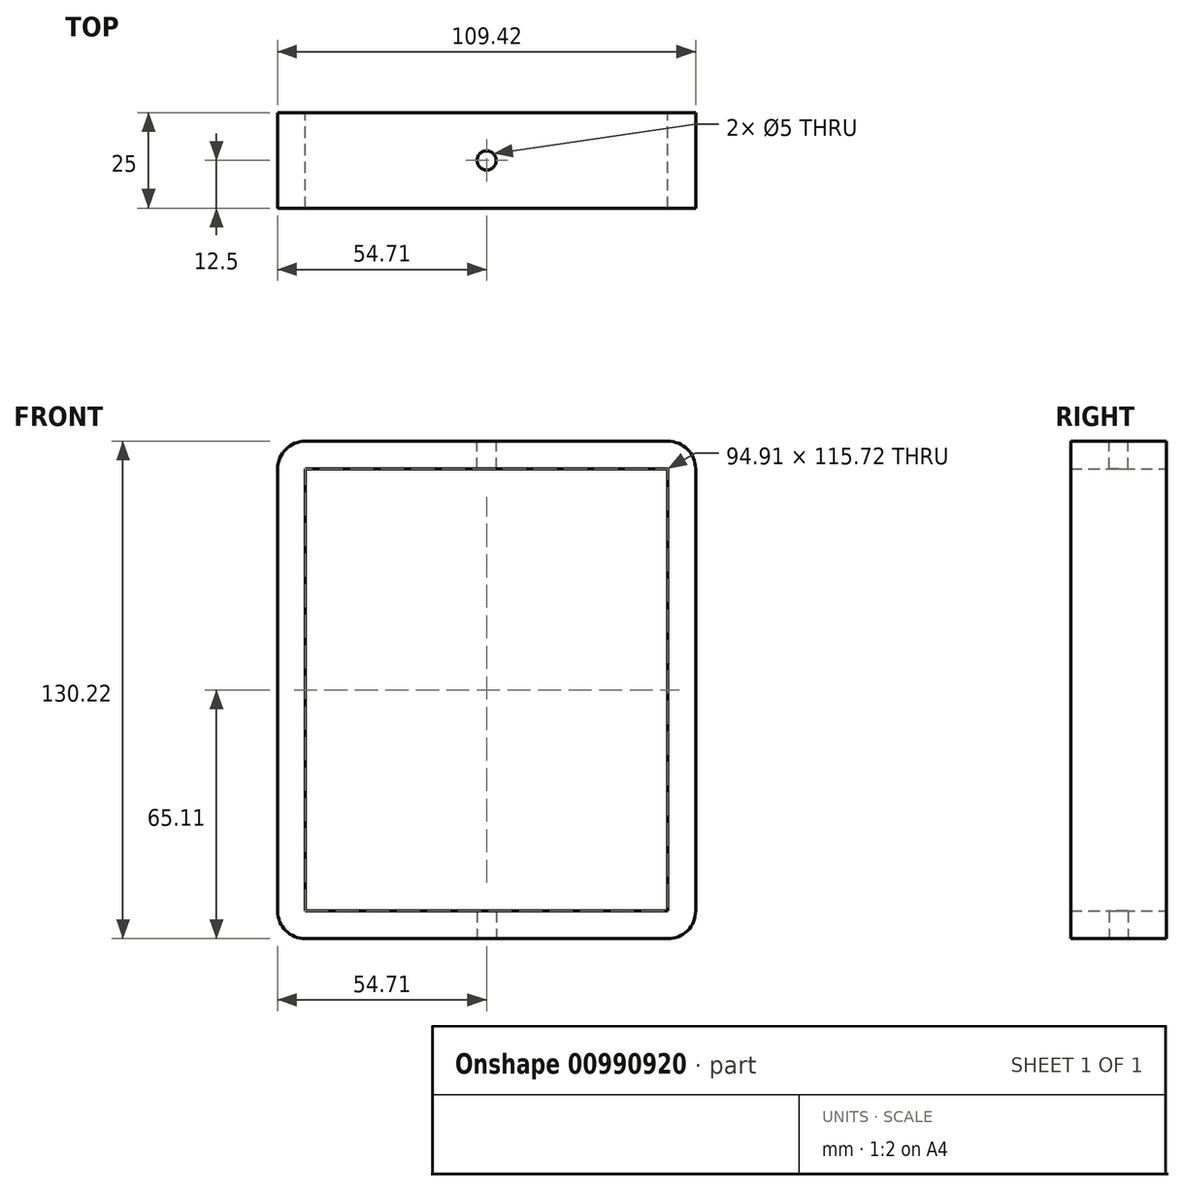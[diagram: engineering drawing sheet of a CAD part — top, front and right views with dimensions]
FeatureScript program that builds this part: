
annotation { "Feature Type Name" : "Feature", "Feature Type Description" : "" }
export const myFeature = defineFeature(function(context is Context, id is Id, definition is map)
    precondition{}
    {
        {
            var Q0;
            Q0=qCreatedBy(makeId("Front.planeOp"),FACE);
            var sketch = newSketch(context, id + "F0", { "sketchPlane" : qUnion([Q0])});
            skLineSegment(sketch, "E0.bottom", {"start": v(47.45, 57.86) * mm, "end": v(-47.45, 57.86) * mm});
            skLineSegment(sketch, "E0.top", {"start": v(47.45, 65.11) * mm, "end": v(-47.45, 65.11) * mm});
            skLineSegment(sketch, "E0.left", {"start": v(47.45, 57.86) * mm, "end": v(47.45, 65.11) * mm});
            skLineSegment(sketch, "E0.right", {"start": v(-47.45, 57.86) * mm, "end": v(-47.45, 65.11) * mm, "construction": true});
            skPoint(sketch, "E0.middle", {"position": v(0, 61.49) * mm});
            skLineSegment(sketch, "E1.MirrorCS", {"start": v(-47.45, -57.86) * mm, "end": v(-47.45, -65.11) * mm});
            skLineSegment(sketch, "E2.MirrorCS", {"start": v(47.45, -65.11) * mm, "end": v(-47.45, -65.11) * mm});
            skLineSegment(sketch, "E3.MirrorCS", {"start": v(47.45, -57.86) * mm, "end": v(47.45, -65.11) * mm, "construction": true});
            skLineSegment(sketch, "E4.MirrorCS", {"start": v(47.45, -57.86) * mm, "end": v(-47.45, -57.86) * mm});
            skArc(sketch, "E5", {"start": v(54.7, -57.86) * mm, "mid": v(52.58, -62.99) * mm, "end": v(47.45, -65.11) * mm});
            skArc(sketch, "E6", {"start": v(-54.7, 57.86) * mm, "mid": v(-52.58, 62.99) * mm, "end": v(-47.45, 65.11) * mm});
            skArc(sketch, "E7", {"start": v(47.45, 65.11) * mm, "mid": v(52.58, 62.99) * mm, "end": v(54.7, 57.86) * mm});
            skArc(sketch, "E8", {"start": v(-47.45, -65.11) * mm, "mid": v(-52.58, -62.99) * mm, "end": v(-54.7, -57.86) * mm});
            skLineSegment(sketch, "E9", {"start": v(-47.45, 57.86) * mm, "end": v(-47.45, -57.86) * mm});
            skLineSegment(sketch, "E10", {"start": v(-54.7, 57.86) * mm, "end": v(-54.7, -57.86) * mm});
            skLineSegment(sketch, "E11", {"start": v(47.45, 57.86) * mm, "end": v(47.45, -57.86) * mm});
            skLineSegment(sketch, "E12", {"start": v(54.7, 57.86) * mm, "end": v(54.7, -57.86) * mm});
            skSolve(sketch);
        }
        {
            var Q0;
            Q0 = qSketchRegion(id + "F0", true);
            extrude(context, id + "F1", {"entities" : qUnion([Q0]), "depth" : 25 * mm, "offsetDistance" : 25 * mm});
        }
        {
            var Q0;
            Q0=makeQuery(id+"F1.opExtrude","SWEPT_FACE",FACE,{"disambiguationData":[OSD([sQuery(id+"F0.wireOp",EDGE,"E0.top")])]});
            var sketch = newSketch(context, id + "F2", { "sketchPlane" : qUnion([Q0])});
            skPoint(sketch, "E13", {"position": v(-47.45, -12.5) * mm});
            skLineSegment(sketch, "E14", {"start": v(-47.45, -12.5) * mm, "end": v(47.45, -12.5) * mm, "construction": true});
            skCircle(sketch, "E15", {"center": v(0, -12.5) * mm, "radius": 2.5 * mm});
            skSolve(sketch);
        }
        {
            var Q0;
            Q0=makeQuery(id+"F1.opExtrude","SWEPT_FACE",FACE,{"disambiguationData":[OSD([sQuery(id+"F0.wireOp",EDGE,"E2.MirrorCS")])]});
            var sketch = newSketch(context, id + "F3", { "sketchPlane" : qUnion([Q0])});
            skLineSegment(sketch, "E16", {"start": v(-47.45, 12.5) * mm, "end": v(47.45, 12.5) * mm, "construction": true});
            skCircle(sketch, "E17", {"center": v(0, 12.5) * mm, "radius": 2.5 * mm});
            skSolve(sketch);
        }
        {
            var Q0;
            Q0=makeQuery(id+"F3.imprint","IMPRINT",FACE,{"disambiguationData":[TD([[makeQuery(id+"F3.imprint","IMPRINT",EDGE,{"derivedFrom":sQuery(id+"F3.wireOp",EDGE,"E17")}),1.0]])]});
            extrude(context, id + "F4", {"entities" : qUnion([Q0]), "operationType" : NewBodyOperationType.REMOVE, "oppositeDirection" : true, "depth" : 25 * mm, "offsetDistance" : 25 * mm});
        }
        {
            var Q0;
            Q0=makeQuery(id+"F2.imprint","IMPRINT",FACE,{"disambiguationData":[TD([[makeQuery(id+"F2.imprint","IMPRINT",EDGE,{"derivedFrom":sQuery(id+"F2.wireOp",EDGE,"E15")}),1.0]])]});
            extrude(context, id + "F5", {"entities" : qUnion([Q0]), "operationType" : NewBodyOperationType.REMOVE, "oppositeDirection" : true, "depth" : 25 * mm, "offsetDistance" : 25 * mm});
        }
    });
